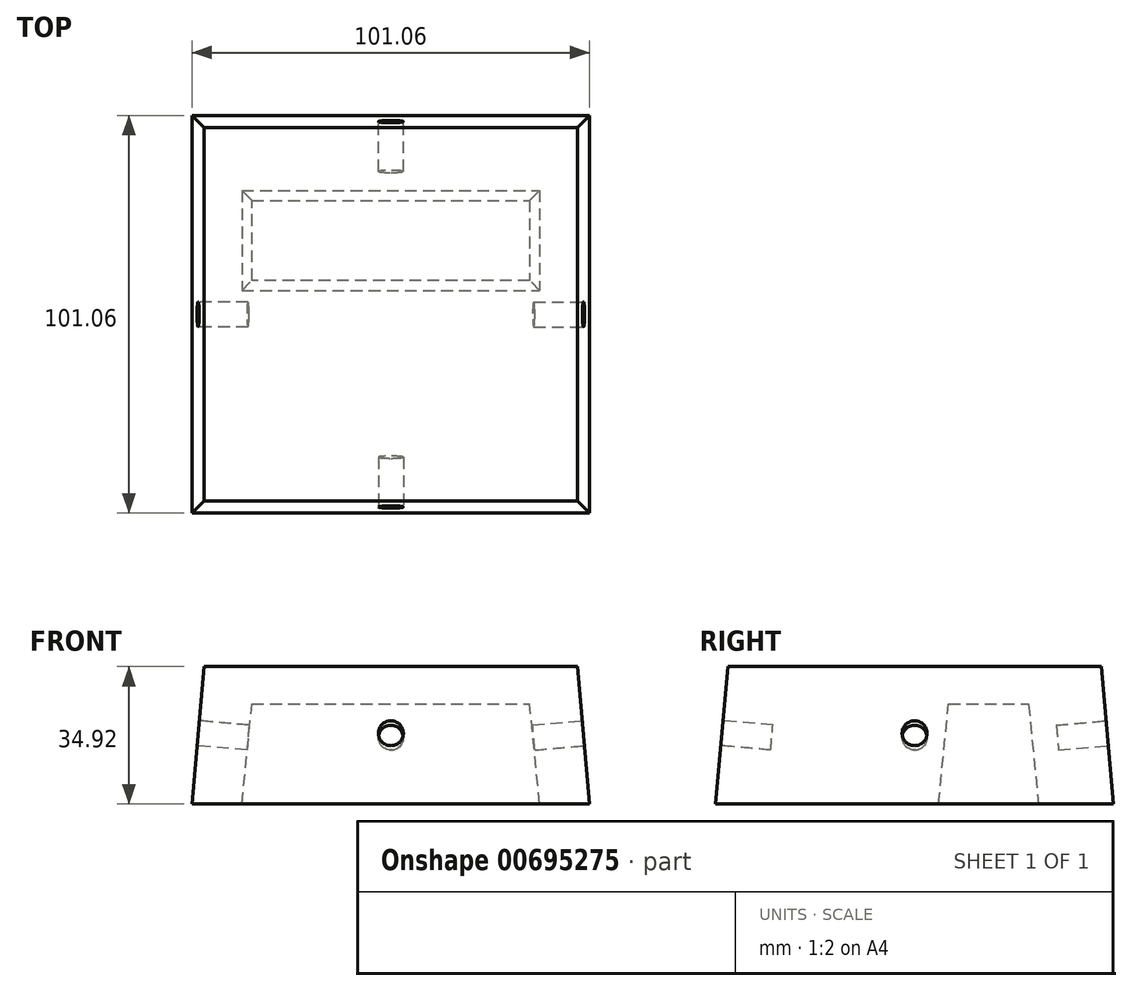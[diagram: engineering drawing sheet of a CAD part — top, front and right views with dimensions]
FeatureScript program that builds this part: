
annotation { "Feature Type Name" : "Feature", "Feature Type Description" : "" }
export const myFeature = defineFeature(function(context is Context, id is Id, definition is map)
    precondition{}
    {
        {
            var Q0;
            Q0=qCreatedBy(makeId("Top.planeOp"),FACE);
            var sketch = newSketch(context, id + "F0", { "sketchPlane" : qUnion([Q0])});
            skLineSegment(sketch, "E0.bottom", {"start": v(-50.8, -50.8) * mm, "end": v(50.8, -50.8) * mm});
            skLineSegment(sketch, "E0.top", {"start": v(-50.8, 50.8) * mm, "end": v(50.8, 50.8) * mm});
            skLineSegment(sketch, "E0.left", {"start": v(-50.8, -50.8) * mm, "end": v(-50.8, 50.8) * mm});
            skLineSegment(sketch, "E0.right", {"start": v(50.8, -50.8) * mm, "end": v(50.8, 50.8) * mm});
            skPoint(sketch, "E0.middle", {"position": v(0, 0) * mm});
            skSolve(sketch);
        }
        {
            var Q0;
            Q0=makeQuery(id+"F0.imprint","IMPRINT",FACE,{"disambiguationData":[TD([[makeQuery(id+"F0.imprint","IMPRINT",EDGE,{"derivedFrom":sQuery(id+"F0.wireOp",EDGE,"E0.bottom")}),1.0]])]});
            extrude(context, id + "F1", {"entities" : qUnion([Q0]), "depth" : 34.92 * mm, "offsetDistance" : 25.4 * mm});
        }
        {
            var Q0;
            Q0=makeQuery(id+"F1.opExtrude","CAP_FACE",FACE,{"disambiguationData":[OSD([sQuery(id+"F0.wireOp",EDGE,"E0.bottom"),sQuery(id+"F0.wireOp",EDGE,"E0.top"),sQuery(id+"F0.wireOp",EDGE,"E0.left"),sQuery(id+"F0.wireOp",EDGE,"E0.right")])],"isStart":false});
            chamfer(context, id + "F2", {"entities" : qUnion([Q0]), "chamferType" : ChamferType.OFFSET_ANGLE, "width" : 3.33 * mm, "oppositeDirection" : false, "angle" : 85 * degree, "tangentPropagation" : true});
        }
        {
            var Q0;
            Q0=makeQuery(id+"F2.opChamfer","BLEND_FACE",FACE,{"disambiguationData":[OSD([sQuery(id+"F0.wireOp",EDGE,"E0.top")])]});
            var sketch = newSketch(context, id + "F3", { "sketchPlane" : qUnion([Q0])});
            skLineSegment(sketch, "E1", {"start": v(50.53, -4.4) * mm, "end": v(-47.47, 30.65) * mm, "construction": true});
            skLineSegment(sketch, "E2", {"start": v(-50.53, -4.4) * mm, "end": v(47.47, 30.65) * mm, "construction": true});
            skCircle(sketch, "E3", {"center": v(0, 13.67) * mm, "radius": 3.18 * mm});
            skSolve(sketch);
        }
        {
            var Q0;
            Q0=makeQuery(id+"F3.imprint","IMPRINT",FACE,{"disambiguationData":[TD([[makeQuery(id+"F3.imprint","IMPRINT",EDGE,{"derivedFrom":sQuery(id+"F3.wireOp",EDGE,"E3")}),1.0]])]});
            extrude(context, id + "F4", {"entities" : qUnion([Q0]), "operationType" : NewBodyOperationType.REMOVE, "oppositeDirection" : true, "depth" : 12.7 * mm, "offsetDistance" : 25.4 * mm});
        }
        {
            var Q0;
            Q0=makeQuery(id+"F2.opChamfer","BLEND_FACE",FACE,{"disambiguationData":[OSD([sQuery(id+"F0.wireOp",EDGE,"E0.right")])]});
            var sketch = newSketch(context, id + "F5", { "sketchPlane" : qUnion([Q0])});
            skLineSegment(sketch, "E4", {"start": v(50.53, -4.4) * mm, "end": v(-47.47, 30.65) * mm, "construction": true});
            skLineSegment(sketch, "E5", {"start": v(-50.53, -4.4) * mm, "end": v(47.47, 30.65) * mm, "construction": true});
            skCircle(sketch, "E6", {"center": v(0, 13.67) * mm, "radius": 3.18 * mm});
            skSolve(sketch);
        }
        {
            var Q0;
            Q0=makeQuery(id+"F5.imprint","IMPRINT",FACE,{"disambiguationData":[TD([[makeQuery(id+"F5.imprint","IMPRINT",EDGE,{"derivedFrom":sQuery(id+"F5.wireOp",EDGE,"E6")}),1.0]])]});
            extrude(context, id + "F6", {"entities" : qUnion([Q0]), "operationType" : NewBodyOperationType.REMOVE, "oppositeDirection" : true, "depth" : 12.7 * mm, "offsetDistance" : 25.4 * mm});
        }
        {
            var Q0;
            Q0=makeQuery(id+"F2.opChamfer","BLEND_FACE",FACE,{"disambiguationData":[OSD([sQuery(id+"F0.wireOp",EDGE,"E0.bottom")])]});
            var sketch = newSketch(context, id + "F7", { "sketchPlane" : qUnion([Q0])});
            skLineSegment(sketch, "E7", {"start": v(50.53, -4.4) * mm, "end": v(-47.47, 30.65) * mm, "construction": true});
            skLineSegment(sketch, "E8", {"start": v(-50.53, -4.4) * mm, "end": v(47.47, 30.65) * mm, "construction": true});
            skCircle(sketch, "E9", {"center": v(0, 13.67) * mm, "radius": 3.18 * mm});
            skSolve(sketch);
        }
        {
            var Q0;
            Q0=makeQuery(id+"F7.imprint","IMPRINT",FACE,{"disambiguationData":[TD([[makeQuery(id+"F7.imprint","IMPRINT",EDGE,{"derivedFrom":sQuery(id+"F7.wireOp",EDGE,"E9")}),1.0]])]});
            extrude(context, id + "F8", {"entities" : qUnion([Q0]), "operationType" : NewBodyOperationType.REMOVE, "oppositeDirection" : true, "depth" : 12.7 * mm, "offsetDistance" : 25.4 * mm});
        }
        {
            var Q0;
            Q0=makeQuery(id+"F2.opChamfer","BLEND_FACE",FACE,{"disambiguationData":[OSD([sQuery(id+"F0.wireOp",EDGE,"E0.left")])]});
            var sketch = newSketch(context, id + "F9", { "sketchPlane" : qUnion([Q0])});
            skLineSegment(sketch, "E10", {"start": v(50.53, -4.4) * mm, "end": v(-47.47, 30.65) * mm, "construction": true});
            skLineSegment(sketch, "E11", {"start": v(47.47, 30.65) * mm, "end": v(-50.53, -4.4) * mm, "construction": true});
            skCircle(sketch, "E12", {"center": v(0, 13.67) * mm, "radius": 3.18 * mm});
            skSolve(sketch);
        }
        {
            var Q0;
            Q0=makeQuery(id+"F9.imprint","IMPRINT",FACE,{"disambiguationData":[TD([[makeQuery(id+"F9.imprint","IMPRINT",EDGE,{"derivedFrom":sQuery(id+"F9.wireOp",EDGE,"E12")}),1.0]])]});
            extrude(context, id + "F10", {"entities" : qUnion([Q0]), "operationType" : NewBodyOperationType.REMOVE, "oppositeDirection" : true, "depth" : 12.7 * mm, "offsetDistance" : 25.4 * mm});
        }
        {
            var Q0;
            Q0=makeQuery(id+"F1.opExtrude","CAP_FACE",FACE,{"disambiguationData":[OSD([sQuery(id+"F0.wireOp",EDGE,"E0.bottom"),sQuery(id+"F0.wireOp",EDGE,"E0.top"),sQuery(id+"F0.wireOp",EDGE,"E0.left"),sQuery(id+"F0.wireOp",EDGE,"E0.right")])],"isStart":true});
            var sketch = newSketch(context, id + "F11", { "sketchPlane" : qUnion([Q0])});
            skLineSegment(sketch, "E13.bottom", {"start": v(-50.53, -50.53) * mm, "end": v(-37.83, -50.53) * mm, "construction": true});
            skLineSegment(sketch, "E13.top", {"start": v(-50.53, -31.48) * mm, "end": v(-37.83, -31.48) * mm, "construction": true});
            skLineSegment(sketch, "E13.left", {"start": v(-50.53, -50.53) * mm, "end": v(-50.53, -31.48) * mm, "construction": true});
            skLineSegment(sketch, "E13.right", {"start": v(-37.83, -50.53) * mm, "end": v(-37.83, -31.48) * mm, "construction": true});
            skLineSegment(sketch, "E14.bottom", {"start": v(50.53, -50.53) * mm, "end": v(37.83, -50.53) * mm, "construction": true});
            skLineSegment(sketch, "E14.top", {"start": v(50.53, -31.48) * mm, "end": v(37.83, -31.48) * mm, "construction": true});
            skLineSegment(sketch, "E14.left", {"start": v(50.53, -50.53) * mm, "end": v(50.53, -31.48) * mm, "construction": true});
            skLineSegment(sketch, "E14.right", {"start": v(37.83, -50.53) * mm, "end": v(37.83, -31.48) * mm, "construction": true});
            skLineSegment(sketch, "E15.bottom", {"start": v(-37.83, -31.48) * mm, "end": v(37.83, -31.48) * mm});
            skLineSegment(sketch, "E15.top", {"start": v(-37.83, -6.08) * mm, "end": v(37.83, -6.08) * mm});
            skLineSegment(sketch, "E15.left", {"start": v(-37.83, -31.48) * mm, "end": v(-37.83, -6.08) * mm});
            skLineSegment(sketch, "E15.right", {"start": v(37.83, -31.48) * mm, "end": v(37.83, -6.08) * mm});
            skSolve(sketch);
        }
        {
            var Q0;
            Q0=makeQuery(id+"F11.imprint","IMPRINT",FACE,{"disambiguationData":[TD([[makeQuery(id+"F11.imprint","IMPRINT",EDGE,{"derivedFrom":sQuery(id+"F11.wireOp",EDGE,"E15.bottom")}),1.0]])]});
            extrude(context, id + "F12", {"entities" : qUnion([Q0]), "operationType" : NewBodyOperationType.REMOVE, "oppositeDirection" : true, "depth" : 25.4 * mm, "offsetDistance" : 25.4 * mm});
        }
        {
            var Q0;
            Q0=makeQuery(id+"F12.boolean.opBoolean","COPY",EDGE,{"derivedFrom":makeQuery(id+"F12.opExtrude","CAP_EDGE",EDGE,{"disambiguationData":[OSD([sQuery(id+"F11.wireOp",EDGE,"E15.top")])],"isStart":false})});
            var Q1;
            Q1=makeQuery(id+"F12.boolean.opBoolean","COPY",EDGE,{"derivedFrom":makeQuery(id+"F12.opExtrude","CAP_EDGE",EDGE,{"disambiguationData":[OSD([sQuery(id+"F11.wireOp",EDGE,"E15.left")])],"isStart":false})});
            var Q2;
            Q2=makeQuery(id+"F12.boolean.opBoolean","COPY",EDGE,{"derivedFrom":makeQuery(id+"F12.opExtrude","CAP_EDGE",EDGE,{"disambiguationData":[OSD([sQuery(id+"F11.wireOp",EDGE,"E15.right")])],"isStart":false})});
            var Q3;
            Q3=makeQuery(id+"F12.boolean.opBoolean","COPY",EDGE,{"derivedFrom":makeQuery(id+"F12.opExtrude","CAP_EDGE",EDGE,{"disambiguationData":[OSD([sQuery(id+"F11.wireOp",EDGE,"E15.bottom")])],"isStart":false})});
            chamfer(context, id + "F13", {"entities" : qUnion([Q0, Q1, Q2, Q3]), "chamferType" : ChamferType.TWO_OFFSETS, "width1" : 25.4 * mm, "oppositeDirection" : false, "width2" : 2.54 * mm, "tangentPropagation" : true});
        }
    });
